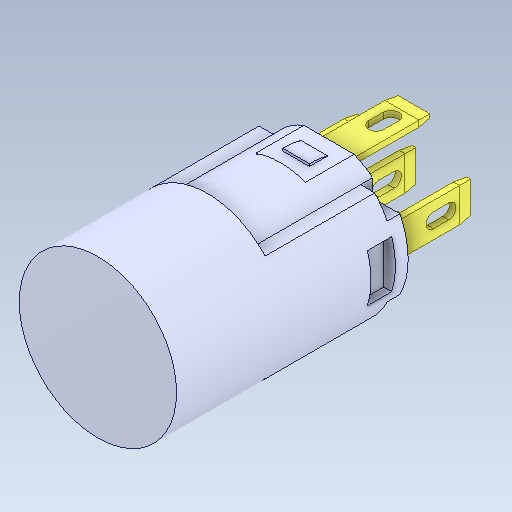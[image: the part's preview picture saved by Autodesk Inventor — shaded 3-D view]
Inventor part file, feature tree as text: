
AUTODESK INVENTOR PART (.ipt)
format: ipt  version: 2020 (Build 240168000, 168)  size: 261,632 bytes
history: mixed  units: mm
features: other x11, mirror x1, imported_body x1
ambient origin geometry x8: Origin, YZ Plane, XZ Plane, XY Plane, X Axis, Y Axis, Z Axis, Center Point
bodies: Body1 (imported_parasolid), Body2 (imported_parasolid), Body3 (imported_parasolid), Body4 (imported_parasolid), Body5 (imported_parasolid), Body6 (imported_parasolid)
feature tree (13):
  other  "Bryła1"
  other  "Bryła2"
  other  "Bryła3"
  other  "Bryła4"
  other  "Bryła5"
  other  "Bryła6"
  other  "Boss-Extrude5[1]"
  other  "Boss-Extrude5[2]"
  other  "Boss-Extrude5[3]"
  other  "Boss-Extrude5[4]"
  other  "Boss-Extrude5[5]"
  mirror  "Mirror1"
  imported_body  NMx_Import_Brep_tag  [imported B-rep: ~203 faces, bbox_mm=[12.620898, 10.95, 26.0]]
